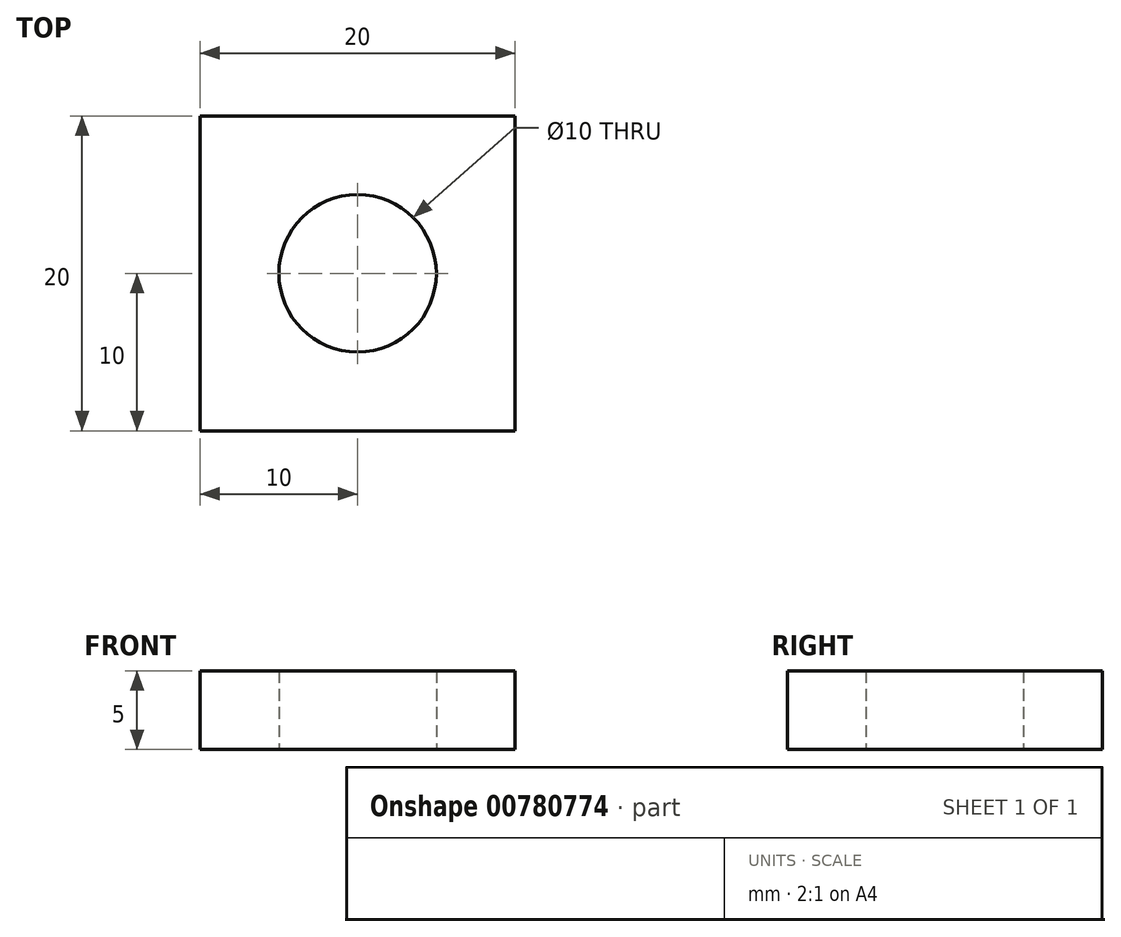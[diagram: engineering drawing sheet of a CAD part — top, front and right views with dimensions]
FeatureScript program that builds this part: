
annotation { "Feature Type Name" : "Feature", "Feature Type Description" : "" }
export const myFeature = defineFeature(function(context is Context, id is Id, definition is map)
    precondition{}
    {
        {
            var Q0;
            Q0=qCreatedBy(makeId("Top.planeOp"),FACE);
            var sketch = newSketch(context, id + "F0", { "sketchPlane" : qUnion([Q0])});
            skLineSegment(sketch, "E0.bottom", {"start": v(-10, 10) * mm, "end": v(10, 10) * mm});
            skLineSegment(sketch, "E0.top", {"start": v(-10, -10) * mm, "end": v(10, -10) * mm});
            skLineSegment(sketch, "E0.left", {"start": v(-10, 10) * mm, "end": v(-10, -10) * mm});
            skLineSegment(sketch, "E0.right", {"start": v(10, 10) * mm, "end": v(10, -10) * mm});
            skPoint(sketch, "E0.middle", {"position": v(0, 0) * mm});
            skCircle(sketch, "E1", {"center": v(0, 0) * mm, "radius": 5 * mm});
            skSolve(sketch);
        }
        {
            var Q0;
            Q0 = qSketchRegion(id + "F0", true);
            extrude(context, id + "F1", {"entities" : qUnion([Q0]), "depth" : 5 * mm, "offsetDistance" : 25 * mm});
        }
    });
